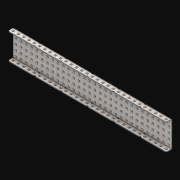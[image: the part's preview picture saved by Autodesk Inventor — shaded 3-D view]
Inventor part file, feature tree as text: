
AUTODESK INVENTOR PART (.ipt)
format: ipt  version: 2021 (Build 250183000, 183)  size: 3,761,152 bytes
history: native  units: in
note: dims shown in document units (in); Inventor stores cm internally (conversion verified against a paired STEP export)
features: extrude x211, other x210, sketch x4, thicken_offset x3, pattern_linear x3, imported_body x1
ambient origin geometry x8: Origin, YZ Plane, XZ Plane, XY Plane, X Axis, Y Axis, Z Axis, Center Point
bodies: Solid1 (feature_tree)
feature tree (432):
  thicken_offset  "Thicken1"
  thicken_offset  "Thicken2"
  thicken_offset  "Thicken3"
  pattern_linear  "Rectangular Pattern1"  Spacing1=0.001in  [1 undecoded]
  pattern_linear  "Rectangular Pattern2"  Spacing1=0.001in  [1 undecoded]
  pattern_linear  "Rectangular Pattern3"  Spacing1=0.182in  [1 undecoded]
  extrude  "Extrusion1"  Depth=0.063in TaperAngle=0.0deg
  sketch  "Sketch1"  dims[d0=0.001in]
  other  "Srf1"
  sketch  "Sketch2"  dims[d1=0.001in]
  other  "Srf2"
  sketch  "Sketch3"  dims[d2=0.001in]
  other  "Srf3"
  other  "Srf4"
  other  "Srf5"
  other  "Srf6"
  other  "Srf7"
  other  "Srf8"
  other  "Srf9"
  other  "Srf10"
  other  "Srf11"
  other  "Srf12"
  other  "Srf13"
  other  "Srf14"
  other  "Srf15"
  other  "Srf16"
  other  "Srf17"
  other  "Srf18"
  other  "Srf19"
  other  "Srf20"
  other  "Srf21"
  other  "Srf22"
  other  "Srf23"
  other  "Srf24"
  other  "Srf25"
  other  "Srf26"
  other  "Srf27"
  other  "Srf28"
  other  "Srf29"
  other  "Srf30"
  other  "Srf31"
  other  "Srf32"
  other  "Srf38"
  other  "Srf39"
  other  "Srf40"
  other  "Srf41"
  other  "Srf42"
  other  "Srf43"
  other  "Srf44"
  other  "Srf45"
  other  "Srf46"
  other  "Srf47"
  other  "Srf48"
  other  "Srf49"
  other  "Srf50"
  other  "Srf51"
  other  "Srf52"
  other  "Srf53"
  other  "Srf54"
  other  "Srf55"
  other  "Srf56"
  other  "Srf57"
  other  "Srf58"
  other  "Srf59"
  other  "Srf60"
  other  "Srf61"
  other  "Srf62"
  other  "Srf63"
  other  "Srf64"
  other  "Srf65"
  other  "Srf66"
  other  "Srf72"
  other  "Srf73"
  other  "Srf74"
  other  "Srf75"
  other  "Srf76"
  other  "Srf77"
  other  "Srf78"
  other  "Srf79"
  other  "Srf80"
  other  "Srf81"
  other  "Srf82"
  other  "Srf83"
  other  "Srf84"
  other  "Srf85"
  other  "Srf86"
  other  "Srf87"
  other  "Srf88"
  other  "Srf89"
  other  "Srf90"
  other  "Srf91"
  other  "Srf92"
  other  "Srf93"
  other  "Srf94"
  other  "Srf95"
  other  "Srf96"
  other  "Srf97"
  other  "Srf98"
  other  "Srf99"
  other  "Srf100"
  other  "Srf106"
  other  "Srf107"
  other  "Srf108"
  other  "Srf109"
  other  "Srf110"
  other  "Srf111"
  other  "Srf112"
  other  "Srf113"
  other  "Srf114"
  other  "Srf115"
  other  "Srf116"
  other  "Srf117"
  other  "Srf118"
  other  "Srf119"
  other  "Srf120"
  other  "Srf121"
  other  "Srf122"
  other  "Srf123"
  other  "Srf124"
  other  "Srf125"
  other  "Srf126"
  other  "Srf127"
  other  "Srf128"
  other  "Srf129"
  other  "Srf130"
  other  "Srf131"
  other  "Srf132"
  other  "Srf133"
  other  "Srf134"
  other  "Srf135"
  other  "Srf141"
  other  "Srf142"
  other  "Srf143"
  other  "Srf144"
  other  "Srf145"
  other  "Srf146"
  other  "Srf147"
  other  "Srf148"
  other  "Srf149"
  other  "Srf150"
  other  "Srf151"
  other  "Srf152"
  other  "Srf153"
  other  "Srf154"
  other  "Srf155"
  other  "Srf156"
  other  "Srf157"
  other  "Srf158"
  other  "Srf159"
  other  "Srf160"
  other  "Srf161"
  other  "Srf162"
  other  "Srf163"
  other  "Srf164"
  other  "Srf165"
  other  "Srf166"
  other  "Srf167"
  other  "Srf168"
  other  "Srf169"
  other  "Srf170"
  other  "Srf176"
  other  "Srf177"
  other  "Srf178"
  other  "Srf179"
  other  "Srf180"
  other  "Srf181"
  other  "Srf182"
  other  "Srf183"
  other  "Srf184"
  other  "Srf185"
  other  "Srf186"
  other  "Srf187"
  other  "Srf188"
  other  "Srf189"
  other  "Srf190"
  other  "Srf191"
  other  "Srf192"
  other  "Srf193"
  other  "Srf194"
  other  "Srf195"
  other  "Srf196"
  other  "Srf197"
  other  "Srf198"
  other  "Srf199"
  other  "Srf200"
  other  "Srf201"
  other  "Srf202"
  other  "Srf203"
  other  "Srf204"
  other  "Srf205"
  other  "Srf211"
  other  "Srf212"
  other  "Srf213"
  other  "Srf214"
  other  "Srf215"
  other  "Srf216"
  other  "Srf217"
  other  "Srf218"
  other  "Srf219"
  other  "Srf220"
  other  "Srf221"
  other  "Srf222"
  other  "Srf223"
  other  "Srf224"
  other  "Srf225"
  other  "Srf226"
  other  "Srf227"
  other  "Srf228"
  other  "Srf229"
  other  "Srf230"
  other  "Srf231"
  other  "Srf232"
  other  "Srf233"
  other  "Srf234"
  other  "Srf235"
  other  "Srf236"
  other  "Srf237"
  other  "Srf238"
  other  "Srf239"
  other  "Srf240"
  sketch  "Sketch4"  dims[d3=0.001in d4=0.001in d5=0.001in d6=0.182in d7=0.063in d8=0.0in d9=0.182in d10=0.063in d11=0.0in d12=0.182in d13=0.063in d14=0.0in d17=0.5in d18=11.811in d20=0.5in d21=11.811in d23=0.5in d24=1.9685in d26=0.5in d27=2.5in d28=0.0in]
  imported_body  "Imported1"
  extrude  "ExtrusionSrf1"  Depth=2.5in
  extrude  "ExtrusionSrf2"  Depth=0.063in TaperAngle=0.0deg
  extrude  "ExtrusionSrf3"  Depth=2.5in
  extrude  "ExtrusionSrf4"  Depth=0.063in TaperAngle=0.0deg
  extrude  "ExtrusionSrf5"  Depth=0.5in
  extrude  "ExtrusionSrf6"  Depth=2.5in
  extrude  "ExtrusionSrf7"  Depth=0.5in
  extrude  "ExtrusionSrf8"  Depth=2.5in
  extrude  "ExtrusionSrf9"  Depth=0.5in
  extrude  "ExtrusionSrf10"  Depth=0.5in
  extrude  "ExtrusionSrf11"  Depth=2.5in
  extrude  "ExtrusionSrf12"  TaperAngle=0.0deg  [1 undecoded]
  extrude  "ExtrusionSrf13"  [1 undecoded]
  extrude  "ExtrusionSrf14"  [1 undecoded]
  extrude  "ExtrusionSrf15"  [1 undecoded]
  extrude  "ExtrusionSrf16"  [1 undecoded]
  extrude  "ExtrusionSrf17"  [1 undecoded]
  extrude  "ExtrusionSrf18"  [1 undecoded]
  extrude  "ExtrusionSrf19"  [1 undecoded]
  extrude  "ExtrusionSrf20"  [1 undecoded]
  extrude  "ExtrusionSrf21"  [1 undecoded]
  extrude  "ExtrusionSrf22"  [1 undecoded]
  extrude  "ExtrusionSrf23"  [1 undecoded]
  extrude  "ExtrusionSrf24"  [1 undecoded]
  extrude  "ExtrusionSrf25"  [1 undecoded]
  extrude  "ExtrusionSrf26"  [1 undecoded]
  extrude  "ExtrusionSrf27"  [1 undecoded]
  extrude  "ExtrusionSrf28"  [1 undecoded]
  extrude  "ExtrusionSrf29"  [1 undecoded]
  extrude  "ExtrusionSrf30"  [1 undecoded]
  extrude  "ExtrusionSrf31"  [1 undecoded]
  extrude  "ExtrusionSrf32"  [1 undecoded]
  extrude  "ExtrusionSrf38"  [1 undecoded]
  extrude  "ExtrusionSrf39"  [1 undecoded]
  extrude  "ExtrusionSrf40"  [1 undecoded]
  extrude  "ExtrusionSrf41"  [1 undecoded]
  extrude  "ExtrusionSrf42"  [1 undecoded]
  extrude  "ExtrusionSrf43"  [1 undecoded]
  extrude  "ExtrusionSrf44"  [1 undecoded]
  extrude  "ExtrusionSrf45"  [1 undecoded]
  extrude  "ExtrusionSrf46"  [1 undecoded]
  extrude  "ExtrusionSrf47"  [1 undecoded]
  extrude  "ExtrusionSrf48"  [1 undecoded]
  extrude  "ExtrusionSrf49"  [1 undecoded]
  extrude  "ExtrusionSrf50"  [1 undecoded]
  extrude  "ExtrusionSrf51"  [1 undecoded]
  extrude  "ExtrusionSrf52"  [1 undecoded]
  extrude  "ExtrusionSrf53"  [1 undecoded]
  extrude  "ExtrusionSrf54"  [1 undecoded]
  extrude  "ExtrusionSrf55"  [1 undecoded]
  extrude  "ExtrusionSrf56"  [1 undecoded]
  extrude  "ExtrusionSrf57"  [1 undecoded]
  extrude  "ExtrusionSrf58"  [1 undecoded]
  extrude  "ExtrusionSrf59"  [1 undecoded]
  extrude  "ExtrusionSrf60"  [1 undecoded]
  extrude  "ExtrusionSrf61"  [1 undecoded]
  extrude  "ExtrusionSrf62"  [1 undecoded]
  extrude  "ExtrusionSrf63"  [1 undecoded]
  extrude  "ExtrusionSrf64"  [1 undecoded]
  extrude  "ExtrusionSrf65"  [1 undecoded]
  extrude  "ExtrusionSrf66"  [1 undecoded]
  extrude  "ExtrusionSrf72"  [1 undecoded]
  extrude  "ExtrusionSrf73"  [1 undecoded]
  extrude  "ExtrusionSrf74"  [1 undecoded]
  extrude  "ExtrusionSrf75"  [1 undecoded]
  extrude  "ExtrusionSrf76"  [1 undecoded]
  extrude  "ExtrusionSrf77"  [1 undecoded]
  extrude  "ExtrusionSrf78"  [1 undecoded]
  extrude  "ExtrusionSrf79"  [1 undecoded]
  extrude  "ExtrusionSrf80"  [1 undecoded]
  extrude  "ExtrusionSrf81"  [1 undecoded]
  extrude  "ExtrusionSrf82"  [1 undecoded]
  extrude  "ExtrusionSrf83"  [1 undecoded]
  extrude  "ExtrusionSrf84"  [1 undecoded]
  extrude  "ExtrusionSrf85"  [1 undecoded]
  extrude  "ExtrusionSrf86"  [1 undecoded]
  extrude  "ExtrusionSrf87"  [1 undecoded]
  extrude  "ExtrusionSrf88"  [1 undecoded]
  extrude  "ExtrusionSrf89"  [1 undecoded]
  extrude  "ExtrusionSrf90"  [1 undecoded]
  extrude  "ExtrusionSrf91"  [1 undecoded]
  extrude  "ExtrusionSrf92"  [1 undecoded]
  extrude  "ExtrusionSrf93"  [1 undecoded]
  extrude  "ExtrusionSrf94"  [1 undecoded]
  extrude  "ExtrusionSrf95"  [1 undecoded]
  extrude  "ExtrusionSrf96"  [1 undecoded]
  extrude  "ExtrusionSrf97"  [1 undecoded]
  extrude  "ExtrusionSrf98"  [1 undecoded]
  extrude  "ExtrusionSrf99"  [1 undecoded]
  extrude  "ExtrusionSrf100"  [1 undecoded]
  extrude  "ExtrusionSrf106"  [1 undecoded]
  extrude  "ExtrusionSrf107"  [1 undecoded]
  extrude  "ExtrusionSrf108"  [1 undecoded]
  extrude  "ExtrusionSrf109"  [1 undecoded]
  extrude  "ExtrusionSrf110"  [1 undecoded]
  extrude  "ExtrusionSrf111"  [1 undecoded]
  extrude  "ExtrusionSrf112"  [1 undecoded]
  extrude  "ExtrusionSrf113"  [1 undecoded]
  extrude  "ExtrusionSrf114"  [1 undecoded]
  extrude  "ExtrusionSrf115"  [1 undecoded]
  extrude  "ExtrusionSrf116"  [1 undecoded]
  extrude  "ExtrusionSrf117"  [1 undecoded]
  extrude  "ExtrusionSrf118"  [1 undecoded]
  extrude  "ExtrusionSrf119"  [1 undecoded]
  extrude  "ExtrusionSrf120"  [1 undecoded]
  extrude  "ExtrusionSrf121"  [1 undecoded]
  extrude  "ExtrusionSrf122"  [1 undecoded]
  extrude  "ExtrusionSrf123"  [1 undecoded]
  extrude  "ExtrusionSrf124"  [1 undecoded]
  extrude  "ExtrusionSrf125"  [1 undecoded]
  extrude  "ExtrusionSrf126"  [1 undecoded]
  extrude  "ExtrusionSrf127"  [1 undecoded]
  extrude  "ExtrusionSrf128"  [1 undecoded]
  extrude  "ExtrusionSrf129"  [1 undecoded]
  extrude  "ExtrusionSrf130"  [1 undecoded]
  extrude  "ExtrusionSrf131"  [1 undecoded]
  extrude  "ExtrusionSrf132"  [1 undecoded]
  extrude  "ExtrusionSrf133"  [1 undecoded]
  extrude  "ExtrusionSrf134"  [1 undecoded]
  extrude  "ExtrusionSrf135"  [1 undecoded]
  extrude  "ExtrusionSrf141"  [1 undecoded]
  extrude  "ExtrusionSrf142"  [1 undecoded]
  extrude  "ExtrusionSrf143"  [1 undecoded]
  extrude  "ExtrusionSrf144"  [1 undecoded]
  extrude  "ExtrusionSrf145"  [1 undecoded]
  extrude  "ExtrusionSrf146"  [1 undecoded]
  extrude  "ExtrusionSrf147"  [1 undecoded]
  extrude  "ExtrusionSrf148"  [1 undecoded]
  extrude  "ExtrusionSrf149"  [1 undecoded]
  extrude  "ExtrusionSrf150"  [1 undecoded]
  extrude  "ExtrusionSrf151"  [1 undecoded]
  extrude  "ExtrusionSrf152"  [1 undecoded]
  extrude  "ExtrusionSrf153"  [1 undecoded]
  extrude  "ExtrusionSrf154"  [1 undecoded]
  extrude  "ExtrusionSrf155"  [1 undecoded]
  extrude  "ExtrusionSrf156"  [1 undecoded]
  extrude  "ExtrusionSrf157"  [1 undecoded]
  extrude  "ExtrusionSrf158"  [1 undecoded]
  extrude  "ExtrusionSrf159"  [1 undecoded]
  extrude  "ExtrusionSrf160"  [1 undecoded]
  extrude  "ExtrusionSrf161"  [1 undecoded]
  extrude  "ExtrusionSrf162"  [1 undecoded]
  extrude  "ExtrusionSrf163"  [1 undecoded]
  extrude  "ExtrusionSrf164"  [1 undecoded]
  extrude  "ExtrusionSrf165"  [1 undecoded]
  extrude  "ExtrusionSrf166"  [1 undecoded]
  extrude  "ExtrusionSrf167"  [1 undecoded]
  extrude  "ExtrusionSrf168"  [1 undecoded]
  extrude  "ExtrusionSrf169"  [1 undecoded]
  extrude  "ExtrusionSrf170"  [1 undecoded]
  extrude  "ExtrusionSrf176"  [1 undecoded]
  extrude  "ExtrusionSrf177"  [1 undecoded]
  extrude  "ExtrusionSrf178"  [1 undecoded]
  extrude  "ExtrusionSrf179"  [1 undecoded]
  extrude  "ExtrusionSrf180"  [1 undecoded]
  extrude  "ExtrusionSrf181"  [1 undecoded]
  extrude  "ExtrusionSrf182"  [1 undecoded]
  extrude  "ExtrusionSrf183"  [1 undecoded]
  extrude  "ExtrusionSrf184"  [1 undecoded]
  extrude  "ExtrusionSrf185"  [1 undecoded]
  extrude  "ExtrusionSrf186"  [1 undecoded]
  extrude  "ExtrusionSrf187"  [1 undecoded]
  extrude  "ExtrusionSrf188"  [1 undecoded]
  extrude  "ExtrusionSrf189"  [1 undecoded]
  extrude  "ExtrusionSrf190"  [1 undecoded]
  extrude  "ExtrusionSrf191"  [1 undecoded]
  extrude  "ExtrusionSrf192"  [1 undecoded]
  extrude  "ExtrusionSrf193"  [1 undecoded]
  extrude  "ExtrusionSrf194"  [1 undecoded]
  extrude  "ExtrusionSrf195"  [1 undecoded]
  extrude  "ExtrusionSrf196"  [1 undecoded]
  extrude  "ExtrusionSrf197"  [1 undecoded]
  extrude  "ExtrusionSrf198"  [1 undecoded]
  extrude  "ExtrusionSrf199"  [1 undecoded]
  extrude  "ExtrusionSrf200"  [1 undecoded]
  extrude  "ExtrusionSrf201"  [1 undecoded]
  extrude  "ExtrusionSrf202"  [1 undecoded]
  extrude  "ExtrusionSrf203"  [1 undecoded]
  extrude  "ExtrusionSrf204"  [1 undecoded]
  extrude  "ExtrusionSrf205"  [1 undecoded]
  extrude  "ExtrusionSrf211"  [1 undecoded]
  extrude  "ExtrusionSrf212"  [1 undecoded]
  extrude  "ExtrusionSrf213"  [1 undecoded]
  extrude  "ExtrusionSrf214"  [1 undecoded]
  extrude  "ExtrusionSrf215"  [1 undecoded]
  extrude  "ExtrusionSrf216"  [1 undecoded]
  extrude  "ExtrusionSrf217"  [1 undecoded]
  extrude  "ExtrusionSrf218"  [1 undecoded]
  extrude  "ExtrusionSrf219"  [1 undecoded]
  extrude  "ExtrusionSrf220"  [1 undecoded]
  extrude  "ExtrusionSrf221"  [1 undecoded]
  extrude  "ExtrusionSrf222"  [1 undecoded]
  extrude  "ExtrusionSrf223"  [1 undecoded]
  extrude  "ExtrusionSrf224"  [1 undecoded]
  extrude  "ExtrusionSrf225"  [1 undecoded]
  extrude  "ExtrusionSrf226"  [1 undecoded]
  extrude  "ExtrusionSrf227"  [1 undecoded]
  extrude  "ExtrusionSrf228"  [1 undecoded]
  extrude  "ExtrusionSrf229"  [1 undecoded]
  extrude  "ExtrusionSrf230"  [1 undecoded]
  extrude  "ExtrusionSrf231"  [1 undecoded]
  extrude  "ExtrusionSrf232"  [1 undecoded]
  extrude  "ExtrusionSrf233"  [1 undecoded]
  extrude  "ExtrusionSrf234"  [1 undecoded]
  extrude  "ExtrusionSrf235"  [1 undecoded]
  extrude  "ExtrusionSrf236"  [1 undecoded]
  extrude  "ExtrusionSrf237"  [1 undecoded]
  extrude  "ExtrusionSrf238"  [1 undecoded]
  extrude  "ExtrusionSrf239"  [1 undecoded]
  extrude  "ExtrusionSrf240"  [1 undecoded]
note: 202 required parameter values undecoded (feature->parameter linkage not recoverable at this tier; creation-order binding heuristic only, values carry confidence <= 0.55)
